# Revit family: 306_H6_N
name_source: partatom
category: Pipe Accessories
units: mm (PartAtom-declared; Revit-internal decimal feet)

## family parameters
Always vertical = Yes
Cut with Voids When Loaded = No
Part Type = Valve - Breaks Into
Round Connector Dimension = Use Diameter
Shared = No
Work Plane-Based = No

## types (15) — shared parameters
CAT0 = Yes
Description = Globe valve, 2-way, Flange, PN 16
L2D_Min = 3048 mm
Manufacturer = Belimo
QmdConnectorList = 301;D;302;D
magiPartTypeId = 306
magiProductFamilyId = H6*N
zero-valued in all types: MC_Default_elevation

## per-type parameters (varying)
| type | BB | BB1 | C | C2 | C__ve | D | DB1 | DB2 | DB3 | DB4 | FD | FD1 | HC | HH1 | HN | HN__ve | L2 | L2D | LM | W2D |
| H611N | 26 mm | 20 mm  [stored 0.0656168 ft] | 14 mm  [stored 0.0459318 ft] | 28 mm  [stored 0.0918635 ft] | -14 mm  [stored -0.0459318 ft] | 15 mm | 38 mm  [stored 0.124672 ft] | 76 mm | 34 mm | 61 mm | 95 mm | 65 mm | 84 mm | 12 mm  [stored 0.0393701 ft] | 5 mm  [stored 0.0164042 ft] | -5 mm  [stored -0.0164042 ft] | 65 mm | 130 mm | 102 mm | 15 mm  [stored 0.0492126 ft] |
| H6100N | 71 mm | 54 mm | 24 mm  [stored 0.0787402 ft] | 48 mm  [stored 0.15748 ft] | -24 mm  [stored -0.0787402 ft] | 100 mm | 132 mm | 264 mm | 119 mm | 211 mm | 220 mm | 158 mm | 172 mm | 33 mm  [stored 0.108268 ft] | 10 mm  [stored 0.0328084 ft] | -10 mm  [stored -0.0328084 ft] | 175 mm | 350 mm | 302 mm | 100 mm |
| H680N | 63 mm | 47 mm | 22 mm  [stored 0.0721785 ft] | 44 mm  [stored 0.144357 ft] | -22 mm  [stored -0.0721785 ft] | 80 mm | 120 mm | 240 mm | 108 mm | 192 mm | 200 mm | 142 mm | 152 mm | 27 mm  [stored 0.0885827 ft] | 10 mm  [stored 0.0328084 ft] | -10 mm  [stored -0.0328084 ft] | 155 mm | 310 mm | 266 mm | 80 mm |
| H679N | 63 mm | 47 mm | 22 mm  [stored 0.0721785 ft] | 44 mm  [stored 0.144357 ft] | -22 mm  [stored -0.0721785 ft] | 80 mm | 120 mm | 240 mm | 108 mm | 192 mm | 200 mm | 142 mm | 152 mm | 27 mm  [stored 0.0885827 ft] | 10 mm  [stored 0.0328084 ft] | -10 mm  [stored -0.0328084 ft] | 155 mm | 310 mm | 266 mm | 80 mm |
| H665N | 57 mm | 43 mm  [stored 0.141076 ft] | 20 mm  [stored 0.0656168 ft] | 40 mm  [stored 0.131234 ft] | -20 mm  [stored -0.0656168 ft] | 65 mm | 93 mm | 185 mm | 83 mm | 148 mm | 185 mm | 130 mm | 140 mm | 25 mm  [stored 0.082021 ft] | 10 mm  [stored 0.0328084 ft] | -10 mm  [stored -0.0328084 ft] | 145 mm | 290 mm | 250 mm | 65 mm |
| H664N | 57 mm | 43 mm  [stored 0.141076 ft] | 20 mm  [stored 0.0656168 ft] | 40 mm  [stored 0.131234 ft] | -20 mm  [stored -0.0656168 ft] | 65 mm | 93 mm | 185 mm | 83 mm | 148 mm | 185 mm | 130 mm | 140 mm | 25 mm  [stored 0.082021 ft] | 10 mm  [stored 0.0328084 ft] | -10 mm  [stored -0.0328084 ft] | 145 mm | 290 mm | 250 mm | 65 mm |
| H650N | 36 mm  [stored 0.11811 ft] | 28 mm  [stored 0.0918635 ft] | 20 mm  [stored 0.0656168 ft] | 40 mm  [stored 0.131234 ft] | -20 mm  [stored -0.0656168 ft] | 50 mm | 66 mm | 132 mm | 59 mm | 106 mm | 165 mm | 114 mm | 120 mm | 15 mm  [stored 0.0492126 ft] | 10 mm  [stored 0.0328084 ft] | -10 mm  [stored -0.0328084 ft] | 115 mm | 230 mm | 190 mm | 50 mm |
| H640N | 36 mm  [stored 0.11811 ft] | 28 mm  [stored 0.0918635 ft] | 18 mm  [stored 0.0590551 ft] | 36 mm  [stored 0.11811 ft] | -18 mm  [stored -0.0590551 ft] | 40 mm | 60 mm | 120 mm | 54 mm | 96 mm | 150 mm | 102 mm | 123 mm | 23 mm  [stored 0.0754593 ft] | 5 mm  [stored 0.0164042 ft] | -5 mm  [stored -0.0164042 ft] | 100 mm | 200 mm | 164 mm | 40 mm  [stored 0.131234 ft] |
| H632N | 32 mm  [stored 0.104987 ft] | 24 mm  [stored 0.0787402 ft] | 18 mm  [stored 0.0590551 ft] | 36 mm  [stored 0.11811 ft] | -18 mm  [stored -0.0590551 ft] | 32 mm | 56 mm | 112 mm | 50 mm | 90 mm | 140 mm | 101 mm | 118 mm | 21 mm | 5 mm  [stored 0.0164042 ft] | -5 mm  [stored -0.0164042 ft] | 90 mm | 180 mm | 144 mm | 32 mm  [stored 0.104987 ft] |
| H625N | 30 mm  [stored 0.0984252 ft] | 22 mm  [stored 0.0721785 ft] | 16 mm  [stored 0.0524934 ft] | 32 mm  [stored 0.104987 ft] | -16 mm  [stored -0.0524934 ft] | 25 mm | 46 mm  [stored 0.150919 ft] | 92 mm | 41 mm | 74 mm | 115 mm | 81 mm | 96 mm | 14 mm  [stored 0.0459318 ft] | 5 mm  [stored 0.0164042 ft] | -5 mm  [stored -0.0164042 ft] | 80 mm | 160 mm | 128 mm | 25 mm  [stored 0.082021 ft] |
| H620N | 26 mm | 20 mm  [stored 0.0656168 ft] | 16 mm  [stored 0.0524934 ft] | 32 mm  [stored 0.104987 ft] | -16 mm  [stored -0.0524934 ft] | 20 mm | 42 mm  [stored 0.137795 ft] | 84 mm | 38 mm  [stored 0.124672 ft] | 67 mm | 105 mm | 73 mm | 91 mm | 11 mm  [stored 0.0360892 ft] | 5 mm  [stored 0.0164042 ft] | -5 mm  [stored -0.0164042 ft] | 75 mm | 150 mm | 118 mm | 20 mm  [stored 0.0656168 ft] |
| H615N | 26 mm | 20 mm  [stored 0.0656168 ft] | 14 mm  [stored 0.0459318 ft] | 28 mm  [stored 0.0918635 ft] | -14 mm  [stored -0.0459318 ft] | 15 mm | 38 mm  [stored 0.124672 ft] | 76 mm | 34 mm | 61 mm | 95 mm | 65 mm | 84 mm | 12 mm  [stored 0.0393701 ft] | 5 mm  [stored 0.0164042 ft] | -5 mm  [stored -0.0164042 ft] | 65 mm | 130 mm | 102 mm | 15 mm  [stored 0.0492126 ft] |
| H614N | 26 mm | 20 mm  [stored 0.0656168 ft] | 14 mm  [stored 0.0459318 ft] | 28 mm  [stored 0.0918635 ft] | -14 mm  [stored -0.0459318 ft] | 15 mm | 38 mm  [stored 0.124672 ft] | 76 mm | 34 mm | 61 mm | 95 mm | 65 mm | 84 mm | 12 mm  [stored 0.0393701 ft] | 5 mm  [stored 0.0164042 ft] | -5 mm  [stored -0.0164042 ft] | 65 mm | 130 mm | 102 mm | 15 mm  [stored 0.0492126 ft] |
| H613N | 26 mm | 20 mm  [stored 0.0656168 ft] | 14 mm  [stored 0.0459318 ft] | 28 mm  [stored 0.0918635 ft] | -14 mm  [stored -0.0459318 ft] | 15 mm | 38 mm  [stored 0.124672 ft] | 76 mm | 34 mm | 61 mm | 95 mm | 65 mm | 84 mm | 12 mm  [stored 0.0393701 ft] | 5 mm  [stored 0.0164042 ft] | -5 mm  [stored -0.0164042 ft] | 65 mm | 130 mm | 102 mm | 15 mm  [stored 0.0492126 ft] |
| H612N | 26 mm | 20 mm  [stored 0.0656168 ft] | 14 mm  [stored 0.0459318 ft] | 28 mm  [stored 0.0918635 ft] | -14 mm  [stored -0.0459318 ft] | 15 mm | 38 mm  [stored 0.124672 ft] | 76 mm | 34 mm | 61 mm | 95 mm | 65 mm | 84 mm | 12 mm  [stored 0.0393701 ft] | 5 mm  [stored 0.0164042 ft] | -5 mm  [stored -0.0164042 ft] | 65 mm | 130 mm | 102 mm | 15 mm  [stored 0.0492126 ft] |

note: column(s) folded — value = type name in every type: magiProductCode, magiProductId

note: [stored X ft] marks values corroborated as IEEE doubles in the binary element streams (Revit-internal decimal feet)

## geometry (parser evidence)
native form markers: Sweep x2
no freeform markers — native parametric forms only
